# Revit family: Mixer_Shower_Nero_Pure
name_source: partatom
category: Plumbing Fixtures
units: mm (PartAtom-declared; Revit-internal decimal feet)

## family parameters
Always vertical = Yes
Cut with Voids When Loaded = Yes
Maintain Annotation Orientation = No
OmniClass Number = 23.31.00.00
Part Type = Normal
Room Calculation Point = No
Round Connector Dimension = Use Diameter
Shared = No
Work Plane-Based = No

## types (4) — shared parameters
Assembly Code = D2010
CW Connection = Yes
HW Connection = Yes
IfcExportAs = IfcSanitaryTerminal
IfcExportType = NOTDEFINED
Manufacturer = Nero
ManufacturerOverallDepth = 62.5 mm  [stored 0.205052 ft]
ManufacturerOverallHeight = 60 mm  [stored 0.19685 ft]
ManufacturerOverallWidth = 60 mm  [stored 0.19685 ft]
ModifiedIssue = 20250123 $
URL = https://nerotapware.com.au
Uniclass2015Code = Pr_40_20_87
Uniclass2015Title = Taps and water supply outlet fittings
Uniclass2015Version = Products v1.35
Vent Connection = No
Waste Connection = No
zero-valued in all types: Default Elevation

## per-type parameters (varying)
| type | BodyMaterial | Description | ManufacturerSpecCode | Model | Type Comments |
| Brushed Gold (NR172211BG) | Metal_Gold_Nero_Brushed | Pure SS316L Shower Mixer Whole Set Brushed Gold | NR172211BG | NR172211BG | Mixer - Shower - Brushed Gold |
| Brushed Nickel (NR172211BN) | Metal_Nickel_Nero_Brushed | Pure SS316L Shower Mixer Whole Set Brushed Nickel | NR172211BN | NR172211BN | Mixer - Shower - Brushed Nickel |
| Brushed Bronze (NR172211BZ) | Metal_Bronze_Nero_Brushed | Pure SS316L Shower Mixer Whole Set Brushed Bronze | NR172211BZ | NR172211BZ | Mixer - Shower - Brushed Bronze |
| Graphite (NR172211GR) | Metal_Graphite_Nero_Brushed | Pure SS316L Shower Mixer Whole Set Graphite | NR172211GR | NR172211GR | Mixer - Shower - Graphite |

note: [stored X ft] marks values corroborated as IEEE doubles in the binary element streams (Revit-internal decimal feet)

## geometry (parser evidence)
native form markers: Sweep x2
no freeform markers — native parametric forms only
